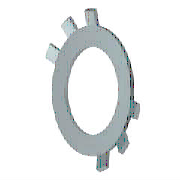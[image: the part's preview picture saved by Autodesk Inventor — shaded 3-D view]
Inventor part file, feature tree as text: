
AUTODESK INVENTOR PART (.ipt)
format: ipt  version: 2020 (Build 240168000, 168)  size: 226,304 bytes
history: native  units: mm (DEFAULTED — no unit token found)
features: extrude x3, other x2, sketch x2, plane x1
ambient origin geometry x8: Origin, YZ Plane, XZ Plane, XY Plane, X Axis, Y Axis, Z Axis, Center Point
bodies: Solid1 (feature_tree)
feature tree (8):
  other  "轴承体"
  sketch  "草图2"  dims[d3=84.0mm d4=100.0mm d5=4.363323mm d6=1.5mm d7=90.0deg d8=65.0mm d9=7.7mm d17=1.5mm d12=0.0mm d13=1.5mm d14=0.0mm d18=0.0mm d20=0.0mm d21=1.5mm d23=6.0mm d24=0.0mm d25=61.0mm d32=7.7mm d34=7.7mm d36=30.0deg d38=3.85mm d39=30.0deg d40=15.0deg d41=7.7mm d42=30.0deg d43=30.0deg d45=7.7mm d47=7.7mm d49=90.0deg d50=0.0mm]
  extrude  "切口"  Depth=1.5mm
  extrude  "榫1"  Depth=7.7mm
  extrude  "榫2"  Depth=7.7mm
  other  "Work Axis1"
  plane  "Work Plane1"
  sketch  "草图1"  dims[d1=1.5mm d2=65.0mm]
